# Revit family: Electronics_Commercial-Audio_Biamp_Wall-Control-Panel_ZONE4R
name_source: partatom
category: Communication Devices
units: mm (PartAtom-declared; Revit-internal decimal feet)

## family parameters
Cut with Voids When Loaded = No
Host = Face
Maintain Annotation Orientation = No
OmniClass Number = 23.85.10.11.14
OmniClass Title = Audio Equipment
Part Type = Normal
Room Calculation Point = No
Round Connector Dimension = Use Diameter
Shared = No

## types (1)
- ZONE4R
    Apparent Load = 0 VA
    Connector Description = +12VDC; Power supply
    Cut-out dimensions in mm = 70 x 55
    Default Elevation = 4' - 0"
    Depth = 0' - 1 1/2"
    Description = ZONE4R ZONE4 Wall Control Panel for Music Level & Source Select
    Display = 2 digit LED
    Height = 0' - 3"
    Housing Material = Biamp - Metal - Silver
    Manufacturer = Biamp
    Max Power Consumption = 0 W
    Max. cable length in m = 100
    Model = ZONE4R
    Number of Poles = 1
    Power Factor = 1
    Power type = Phantom
    Product Documentation Link = https://downloads.biamp.com
    Product Page URL = https://www.biamp.com
    Product data url = https://www.bimobject.com
    Supported main unit = ZONE4
    URL = https://www.biamp.com
    Voltage = 0 V
    Weight = 0.31 lb
    Width = 0' - 4 1/2"

## geometry (parser evidence)
native form markers: Blend x2, Sweep x3
no freeform markers — native parametric forms only
